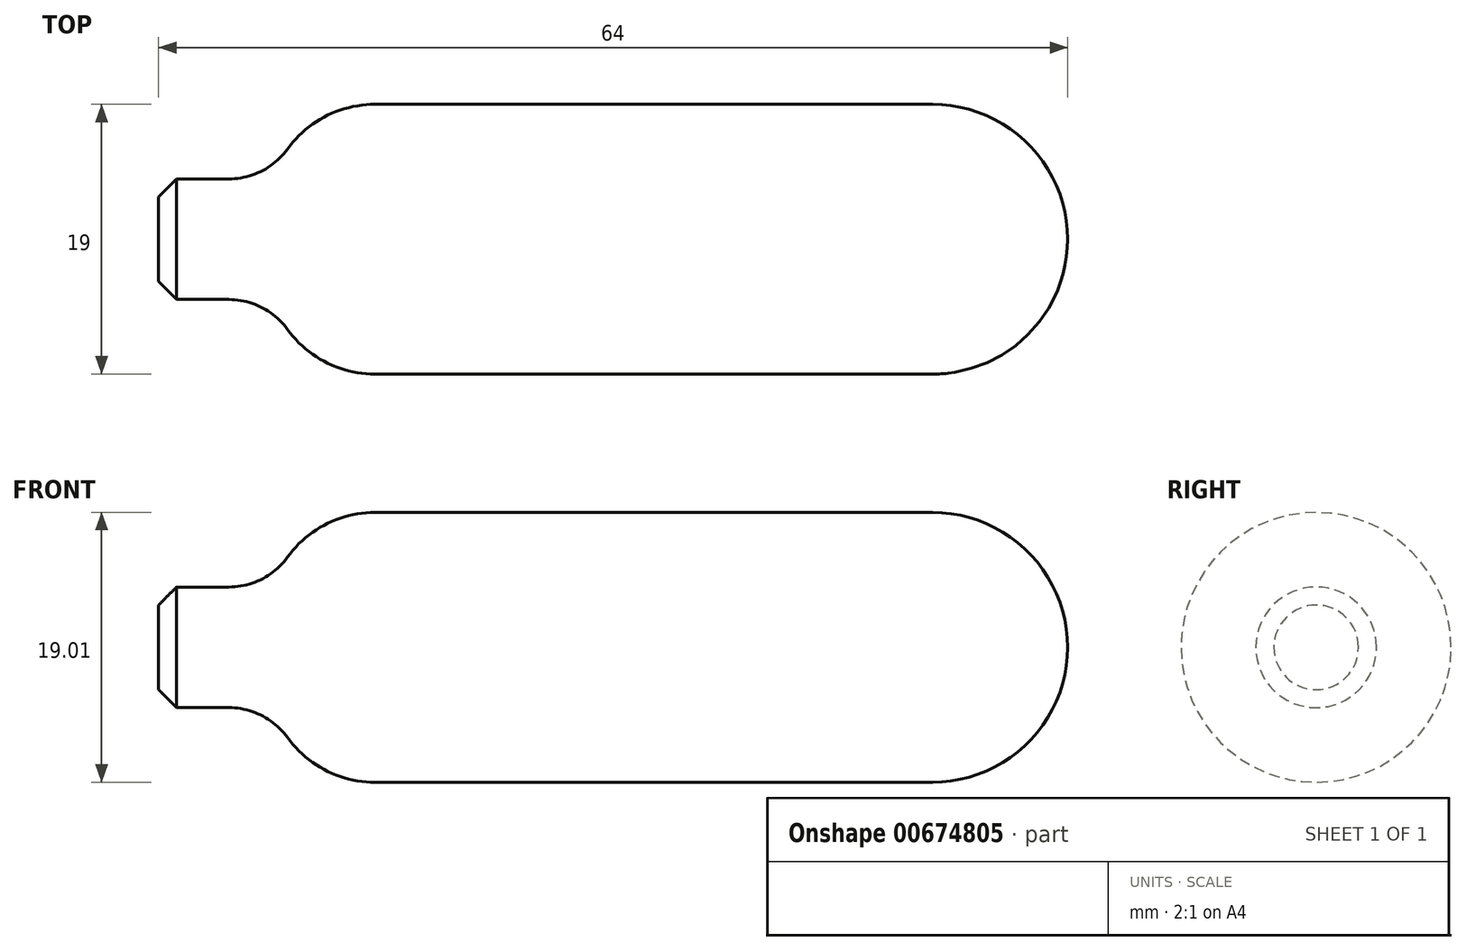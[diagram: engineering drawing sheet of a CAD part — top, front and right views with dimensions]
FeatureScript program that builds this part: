
annotation { "Feature Type Name" : "Feature", "Feature Type Description" : "" }
export const myFeature = defineFeature(function(context is Context, id is Id, definition is map)
    precondition{}
    {
        {
            var Q0;
            Q0=qCreatedBy(makeId("Front.planeOp"),FACE);
            var sketch = newSketch(context, id + "F0", { "sketchPlane" : qUnion([Q0])});
            skLineSegment(sketch, "E0", {"start": v(-65.91, 18.16) * mm, "end": v(-1.91, 18.16) * mm});
            skLineSegment(sketch, "E1", {"start": v(-65.91, 18.16) * mm, "end": v(-65.91, 22.41) * mm});
            skLineSegment(sketch, "E2", {"start": v(-65.91, 22.41) * mm, "end": v(-57.91, 22.41) * mm});
            skLineSegment(sketch, "E3", {"start": v(-1.91, 18.16) * mm, "end": v(-1.91, 18.17) * mm});
            skLineSegment(sketch, "E4", {"start": v(-57.91, 22.41) * mm, "end": v(-57.91, 27.67) * mm});
            skPoint(sketch, "E5.visualSharp", {"position": v(-1.91, 27.66) * mm});
            skArc(sketch, "E5.filletArc", {"start": v(-1.91, 18.17) * mm, "mid": v(-4.7, 24.88) * mm, "end": v(-11.41, 27.67) * mm});
            skLineSegment(sketch, "E6", {"start": v(-57.91, 27.67) * mm, "end": v(-11.41, 27.67) * mm});
            skSolve(sketch);
        }
        {
            var Q0;
            Q0 = qSketchRegion(id + "F0", true);
            var Q1;
            Q1=sQuery(id+"F0.wireOp",EDGE,"E0");
            revolve(context, id + "F1", {"entities" : qUnion([Q0]), "axis" : qUnion([Q1]), "revolveType" : RevolveType.FULL});
        }
        {
            var Q0;
            Q0=makeQuery(id+"F1.opRevolve","SWEPT_EDGE",EDGE,{"disambiguationData":[OSD([sQuery(id+"F0.wireOp",EDGE,"E4"),sQuery(id+"F0.wireOp",EDGE,"E6")])]});
            fillet(context, id + "F2", {"entities" : qUnion([Q0]), "radius" : 7.62 * mm, "allowEdgeOverflow" : false});
        }
        {
            var Q0;
            Q0=makeQuery(id+"F2.opFillet","BLEND_EDGE",EDGE,{"blendedFrom":[makeQuery(id+"F1.opRevolve","SWEPT_EDGE",EDGE,{"disambiguationData":[OSD([sQuery(id+"F0.wireOp",EDGE,"E4"),sQuery(id+"F0.wireOp",EDGE,"E6")])]}),makeQuery(id+"F1.opRevolve","SWEPT_FACE",FACE,{"disambiguationData":[OSD([sQuery(id+"F0.wireOp",EDGE,"E2")])]})],"blendedInto":[makeQuery(id+"F1.opRevolve","SWEPT_FACE",FACE,{"disambiguationData":[OSD([sQuery(id+"F0.wireOp",EDGE,"E2")])]})]});
            fillet(context, id + "F3", {"entities" : qUnion([Q0]), "radius" : 5.08 * mm, "tangentPropagation" : true, "allowEdgeOverflow" : false});
        }
        {
            var Q0;
            Q0=makeQuery(id+"F1.opRevolve","SWEPT_EDGE",EDGE,{"disambiguationData":[OSD([sQuery(id+"F0.wireOp",EDGE,"E1"),sQuery(id+"F0.wireOp",EDGE,"E2")])]});
            chamfer(context, id + "F4", {"entities" : qUnion([Q0]), "width" : 1.27 * mm, "tangentPropagation" : true});
        }
    });
